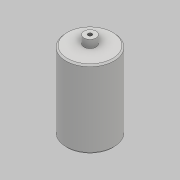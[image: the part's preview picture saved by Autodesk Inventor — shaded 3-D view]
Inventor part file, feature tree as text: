
AUTODESK INVENTOR PART (.ipt)
format: ipt  version: 2018 (Build 220112000, 112)  size: 113,152 bytes
history: native  units: mm
features: other x2, mirror x2, plane x2, chamfer x1, hole x1, sketch x1
ambient origin geometry x8: Origin, YZ Plane, XZ Plane, XY Plane, X Axis, Y Axis, Z Axis, Center Point
bodies: Body1 (feature_tree)
feature tree (9):
  other  "實體1"
  other  "迴轉1"
  mirror  "鏡射1"
  chamfer  "倒角1"  Distance=100.0mm
  hole  "孔1"  [1 undecoded]
  plane  "工作平面1"
  plane  "工作平面2"
  mirror  "鏡射2"
  sketch  "草圖1"
note: 1 required parameter value undecoded (feature->parameter linkage not recoverable at this tier; creation-order binding heuristic only, values carry confidence <= 0.55)
